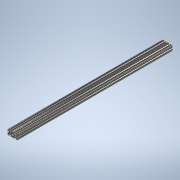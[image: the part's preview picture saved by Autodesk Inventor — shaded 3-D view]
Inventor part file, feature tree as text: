
AUTODESK INVENTOR PART (.ipt)
format: ipt  version: 2020 (Build 240168000, 168)  size: 358,912 bytes
history: native  units: in
note: dims shown in document units (in); Inventor stores cm internally (conversion verified against a paired STEP export)
features: sketch x2, extrude x1
ambient origin geometry x8: Origin, YZ Plane, XZ Plane, XY Plane, X Axis, Y Axis, Z Axis, Center Point
bodies: Solid1 (feature_tree)
feature tree (3):
  extrude  "Extrusion1"  [1 undecoded]
  sketch  "Sketch2"
  sketch  "Sketch1"  dims[d0=31.0in d1=0.0in]
note: 1 required parameter value undecoded (feature->parameter linkage not recoverable at this tier; creation-order binding heuristic only, values carry confidence <= 0.55)
